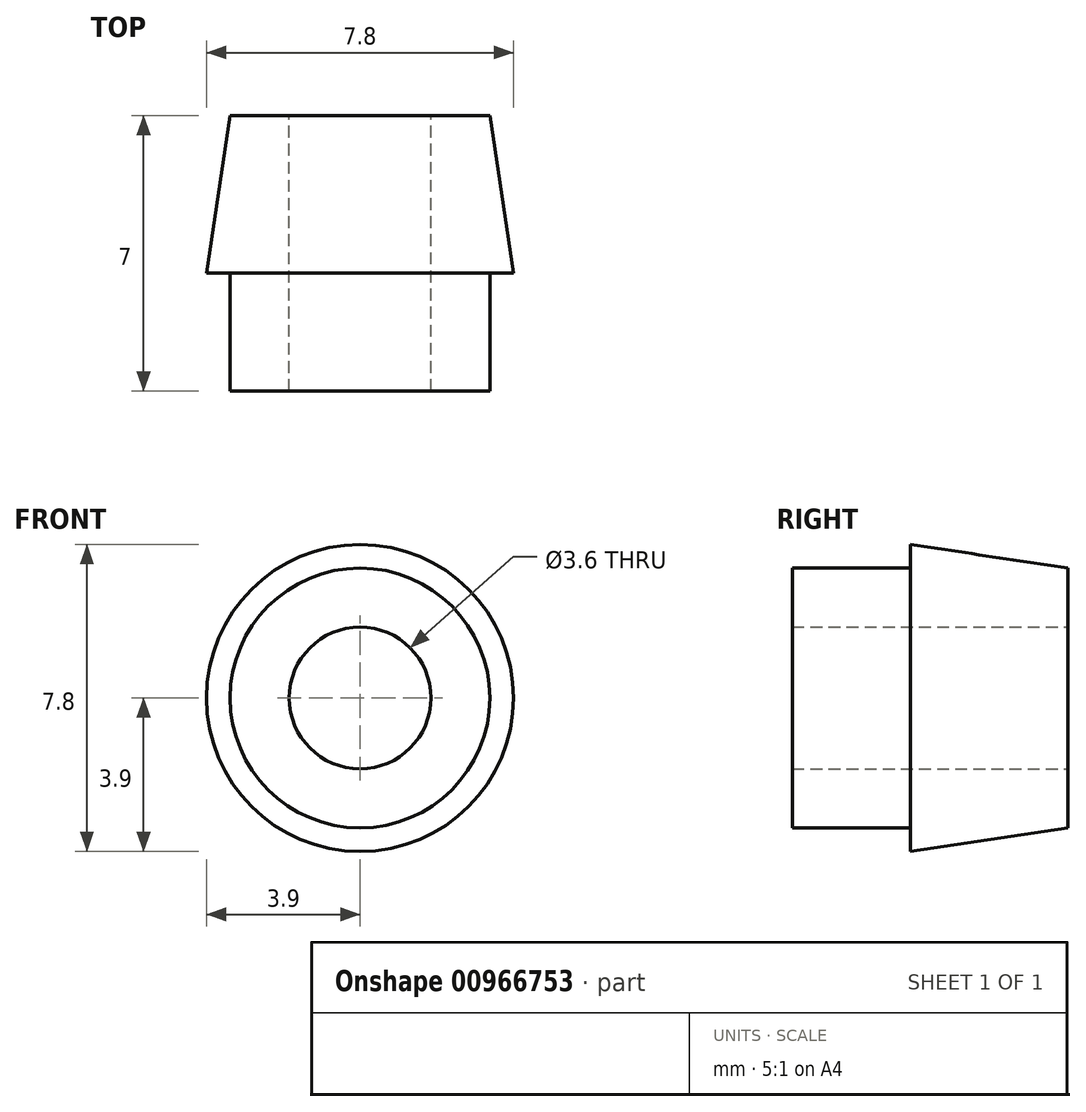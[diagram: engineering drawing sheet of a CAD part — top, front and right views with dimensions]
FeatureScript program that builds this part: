
annotation { "Feature Type Name" : "Feature", "Feature Type Description" : "" }
export const myFeature = defineFeature(function(context is Context, id is Id, definition is map)
    precondition{}
    {
        {
            var Q0;
            Q0=qCreatedBy(makeId("Top.planeOp"),FACE);
            var sketch = newSketch(context, id + "F0", { "sketchPlane" : qUnion([Q0])});
            skLineSegment(sketch, "E0", {"start": v(0, 0) * mm, "end": v(-3.3, 0) * mm});
            skLineSegment(sketch, "E1", {"start": v(-3.3, 0) * mm, "end": v(-3.3, 3) * mm});
            skLineSegment(sketch, "E2", {"start": v(-3.9, 3) * mm, "end": v(-3.3, 3) * mm});
            skLineSegment(sketch, "E3", {"start": v(-3.9, 3) * mm, "end": v(-3.3, 7) * mm});
            skLineSegment(sketch, "E4", {"start": v(-3.3, 7) * mm, "end": v(0, 7) * mm});
            skLineSegment(sketch, "E5", {"start": v(0, 7) * mm, "end": v(0, 0) * mm});
            skSolve(sketch);
        }
        {
            var Q0;
            Q0=makeQuery(id+"F0.imprint","IMPRINT",FACE,{"disambiguationData":[TD([[makeQuery(id+"F0.imprint","IMPRINT",EDGE,{"derivedFrom":sQuery(id+"F0.wireOp",EDGE,"E0")}),-1.0]])]});
            var Q1;
            Q1=sQuery(id+"F0.wireOp",EDGE,"E5");
            revolve(context, id + "F1", {"surfaceOperationType" : NewSurfaceOperationType.NEW, "entities" : qUnion([Q0]), "axis" : qUnion([Q1]), "revolveType" : RevolveType.FULL});
        }
        {
            var Q0;
            Q0=makeQuery(id+"F1.opRevolve","SWEPT_FACE",FACE,{"disambiguationData":[OSD([sQuery(id+"F0.wireOp",EDGE,"E4")])]});
            var sketch = newSketch(context, id + "F2", { "sketchPlane" : qUnion([Q0])});
            skCircle(sketch, "E6", {"center": v(0, 0) * mm, "radius": 1.8 * mm});
            skSolve(sketch);
        }
        {
            var Q0;
            Q0=makeQuery(id+"F2.imprint","IMPRINT",FACE,{"disambiguationData":[TD([[makeQuery(id+"F2.imprint","IMPRINT",EDGE,{"derivedFrom":sQuery(id+"F2.wireOp",EDGE,"E6")}),1.0]])]});
            extrude(context, id + "F3", {"entities" : qUnion([Q0]), "operationType" : NewBodyOperationType.REMOVE, "endBound" : BoundingType.THROUGH_ALL, "oppositeDirection" : true, "depth" : 25 * mm, "offsetDistance" : 25 * mm});
        }
    });
